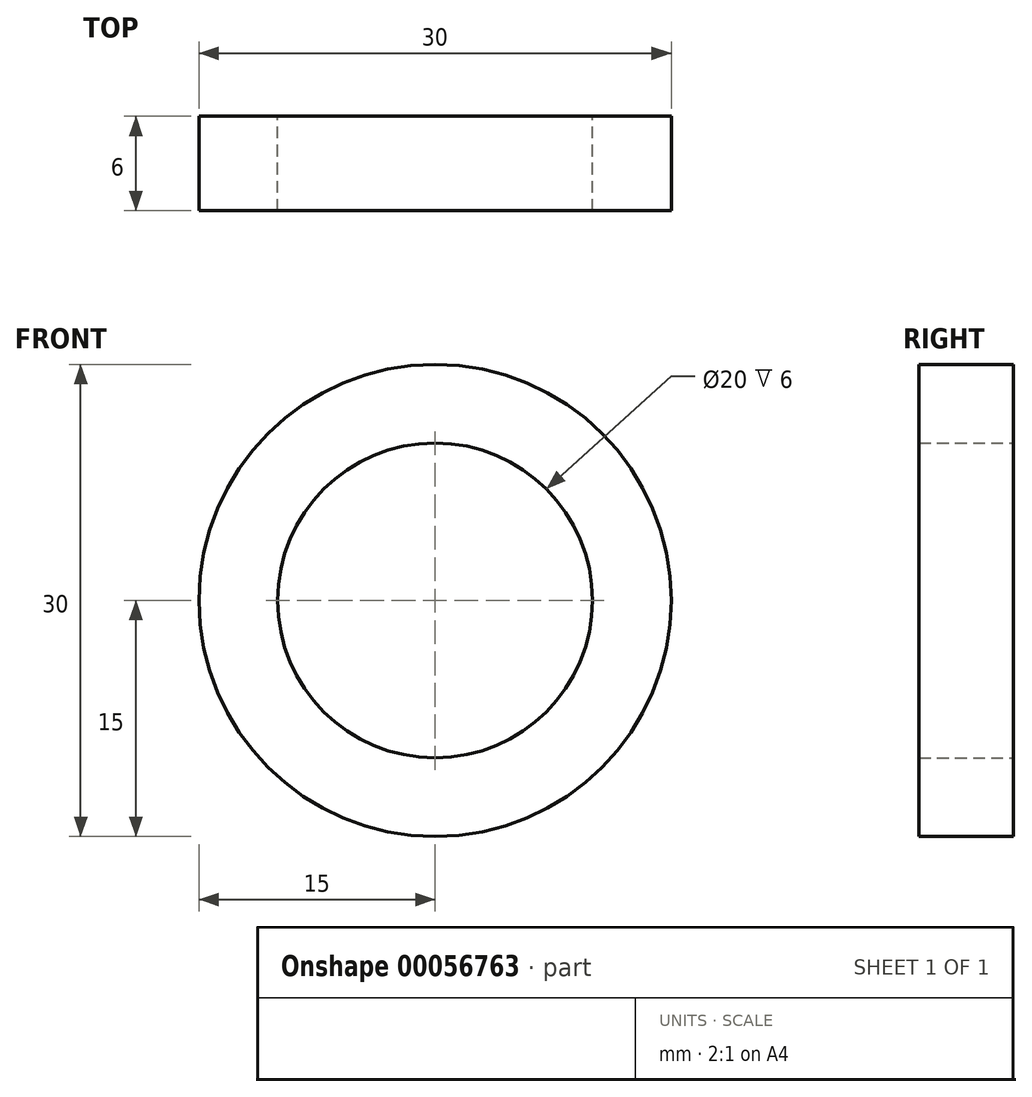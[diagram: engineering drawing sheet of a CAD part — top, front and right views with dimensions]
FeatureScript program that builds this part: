
annotation { "Feature Type Name" : "Feature", "Feature Type Description" : "" }
export const myFeature = defineFeature(function(context is Context, id is Id, definition is map)
    precondition{}
    {
        {
            var Q0;
            Q0=qCreatedBy(makeId("Front.planeOp"),FACE);
            var sketch = newSketch(context, id + "F0", { "sketchPlane" : qUnion([Q0])});
            skCircle(sketch, "E0", {"center": v(0, 0) * mm, "radius": 15 * mm});
            skCircle(sketch, "E1", {"center": v(0, 0) * mm, "radius": 10 * mm});
            skSolve(sketch);
        }
        {
            var Q0;
            Q0 = qSketchRegion(id + "F0", true);
            extrude(context, id + "F1", {"entities" : qUnion([Q0]), "depth" : 6 * mm});
        }
    });
